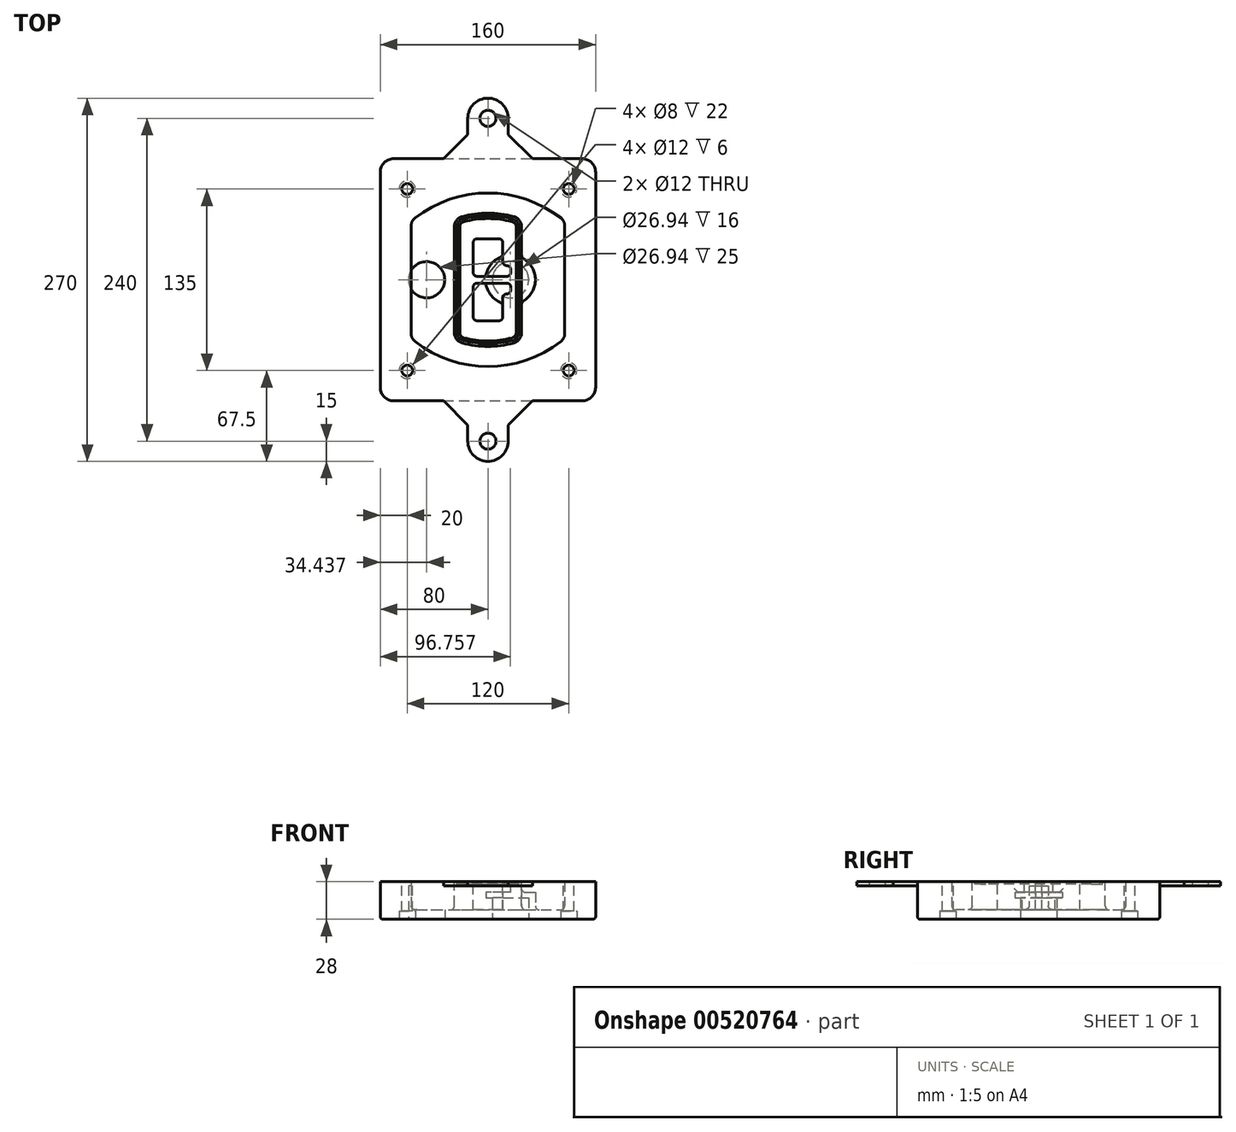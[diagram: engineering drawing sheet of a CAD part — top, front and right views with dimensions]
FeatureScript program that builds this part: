
annotation { "Feature Type Name" : "Feature", "Feature Type Description" : "" }
export const myFeature = defineFeature(function(context is Context, id is Id, definition is map)
    precondition{}
    {
        {
            var Q0;
            Q0=qCreatedBy(makeId("Top.planeOp"),FACE);
            var sketch = newSketch(context, id + "F0", { "sketchPlane" : qUnion([Q0])});
            skPoint(sketch, "E0.rect.middle", {"position": v(0, 0) * mm});
            skLineSegment(sketch, "E1.bottom", {"start": v(-70, -90) * mm, "end": v(70, -90) * mm});
            skLineSegment(sketch, "E1.top", {"start": v(-70, 90) * mm, "end": v(70, 90) * mm});
            skLineSegment(sketch, "E1.left", {"start": v(-80, -80) * mm, "end": v(-80, 80) * mm});
            skLineSegment(sketch, "E1.right", {"start": v(80, -80) * mm, "end": v(80, 80) * mm});
            skLineSegment(sketch, "E2", {"start": v(-80, 90) * mm, "end": v(80, -90) * mm, "construction": true});
            skLineSegment(sketch, "E3", {"start": v(80, 90) * mm, "end": v(-80, -90) * mm, "construction": true});
            skCircle(sketch, "E4", {"center": v(-60, 67.5) * mm, "radius": 4 * mm});
            skCircle(sketch, "E5", {"center": v(60, 67.5) * mm, "radius": 4 * mm});
            skCircle(sketch, "E6", {"center": v(60, -67.5) * mm, "radius": 4 * mm});
            skCircle(sketch, "E7", {"center": v(-60, -67.5) * mm, "radius": 4 * mm});
            skLineSegment(sketch, "E8", {"start": v(-60, 67.5) * mm, "end": v(60, 67.5) * mm, "construction": true});
            skLineSegment(sketch, "E9", {"start": v(60, 67.5) * mm, "end": v(60, -67.5) * mm, "construction": true});
            skLineSegment(sketch, "E10", {"start": v(60, -67.5) * mm, "end": v(-60, -67.5) * mm, "construction": true});
            skLineSegment(sketch, "E11", {"start": v(-60, -67.5) * mm, "end": v(-60, 67.5) * mm, "construction": true});
            skLineSegment(sketch, "E12", {"start": v(-60, 40.3) * mm, "end": v(-60, -40.3) * mm});
            skLineSegment(sketch, "E13", {"start": v(60, 40.3) * mm, "end": v(60, -40.3) * mm});
            skArc(sketch, "E14", {"start": v(56.15, 48.18) * mm, "mid": v(0, 67.5) * mm, "end": v(-56.15, 48.18) * mm});
            skArc(sketch, "E15", {"start": v(-56.15, -48.18) * mm, "mid": v(0, -67.5) * mm, "end": v(56.15, -48.18) * mm});
            skLineSegment(sketch, "E16", {"start": v(-60, 0) * mm, "end": v(60, 0) * mm, "construction": true});
            skPoint(sketch, "E17.visualSharp", {"position": v(-60, -45) * mm});
            skArc(sketch, "E17.filletArc", {"start": v(-60, -40.3) * mm, "mid": v(-58.99, -44.68) * mm, "end": v(-56.15, -48.18) * mm});
            skPoint(sketch, "E18.visualSharp", {"position": v(-60, 45) * mm});
            skArc(sketch, "E18.filletArc", {"start": v(-56.15, 48.18) * mm, "mid": v(-58.99, 44.68) * mm, "end": v(-60, 40.3) * mm});
            skPoint(sketch, "E19.visualSharp", {"position": v(60, 45) * mm});
            skArc(sketch, "E19.filletArc", {"start": v(60, 40.3) * mm, "mid": v(58.99, 44.68) * mm, "end": v(56.15, 48.18) * mm});
            skPoint(sketch, "E20.visualSharp", {"position": v(60, -45) * mm});
            skArc(sketch, "E20.filletArc", {"start": v(56.15, -48.18) * mm, "mid": v(58.99, -44.68) * mm, "end": v(60, -40.3) * mm});
            skPoint(sketch, "E21.visualSharp", {"position": v(-80, 90) * mm});
            skArc(sketch, "E21.filletArc", {"start": v(-70, 90) * mm, "mid": v(-77.07, 87.07) * mm, "end": v(-80, 80) * mm});
            skPoint(sketch, "E22.visualSharp", {"position": v(80, 90) * mm});
            skArc(sketch, "E22.filletArc", {"start": v(80, 80) * mm, "mid": v(77.07, 87.07) * mm, "end": v(70, 90) * mm});
            skPoint(sketch, "E23.visualSharp", {"position": v(80, -90) * mm});
            skArc(sketch, "E23.filletArc", {"start": v(70, -90) * mm, "mid": v(77.07, -87.07) * mm, "end": v(80, -80) * mm});
            skPoint(sketch, "E24.visualSharp", {"position": v(-80, -90) * mm});
            skArc(sketch, "E24.filletArc", {"start": v(-80, -80) * mm, "mid": v(-77.07, -87.07) * mm, "end": v(-70, -90) * mm});
            skArc(sketch, "E25.0", {"start": v(57, 40.3) * mm, "mid": v(56.3, 43.36) * mm, "end": v(54.3, 45.81) * mm});
            skLineSegment(sketch, "E25.1", {"start": v(57, 40.3) * mm, "end": v(57, -40.3) * mm});
            skArc(sketch, "E25.2", {"start": v(54.3, -45.81) * mm, "mid": v(56.3, -43.36) * mm, "end": v(57, -40.3) * mm});
            skArc(sketch, "E25.3", {"start": v(-54.3, -45.81) * mm, "mid": v(0, -64.5) * mm, "end": v(54.3, -45.81) * mm});
            skArc(sketch, "E25.4", {"start": v(-57, -40.3) * mm, "mid": v(-56.3, -43.36) * mm, "end": v(-54.3, -45.81) * mm});
            skArc(sketch, "E25.5", {"start": v(54.3, 45.81) * mm, "mid": v(0, 64.5) * mm, "end": v(-54.3, 45.81) * mm});
            skLineSegment(sketch, "E25.6", {"start": v(-57, 40.3) * mm, "end": v(-57, -40.3) * mm});
            skArc(sketch, "E25.7", {"start": v(-54.3, 45.81) * mm, "mid": v(-56.3, 43.36) * mm, "end": v(-57, 40.3) * mm});
            skArc(sketch, "E26.0", {"start": v(-58.62, 51.33) * mm, "mid": v(-62.58, 46.43) * mm, "end": v(-64, 40.3) * mm});
            skArc(sketch, "E26.1", {"start": v(58.62, 51.33) * mm, "mid": v(0, 71.5) * mm, "end": v(-58.62, 51.33) * mm});
            skArc(sketch, "E26.2", {"start": v(64, 40.3) * mm, "mid": v(62.58, 46.43) * mm, "end": v(58.62, 51.33) * mm});
            skLineSegment(sketch, "E26.3", {"start": v(64, 40.3) * mm, "end": v(64, -40.3) * mm});
            skArc(sketch, "E26.4", {"start": v(58.62, -51.33) * mm, "mid": v(62.58, -46.43) * mm, "end": v(64, -40.3) * mm});
            skLineSegment(sketch, "E26.5", {"start": v(-64, 40.3) * mm, "end": v(-64, -40.3) * mm});
            skArc(sketch, "E26.6", {"start": v(-58.62, -51.33) * mm, "mid": v(0, -71.5) * mm, "end": v(58.62, -51.33) * mm});
            skArc(sketch, "E26.7", {"start": v(-64, -40.3) * mm, "mid": v(-62.58, -46.43) * mm, "end": v(-58.62, -51.33) * mm});
            skSolve(sketch);
        }
        {
            var Q0;
            Q0=makeQuery(id+"F0.imprint","IMPRINT",FACE,{"disambiguationData":[TD([[makeQuery(id+"F0.imprint","IMPRINT",EDGE,{"derivedFrom":sQuery(id+"F0.wireOp",EDGE,"E1.bottom")}),1.0]])]});
            var Q1;
            Q1=makeQuery(id+"F0.imprint","IMPRINT",FACE,{"disambiguationData":[TD([[makeQuery(id+"F0.imprint","IMPRINT",EDGE,{"derivedFrom":sQuery(id+"F0.wireOp",EDGE,"E12")}),1.0]])]});
            var Q2;
            Q2=makeQuery(id+"F0.imprint","IMPRINT",FACE,{"disambiguationData":[TD([[makeQuery(id+"F0.imprint","IMPRINT",EDGE,{"derivedFrom":sQuery(id+"F0.wireOp",EDGE,"E25.0")}),1.0]])]});
            var Q3;
            Q3=makeQuery(id+"F0.imprint","IMPRINT",FACE,{"disambiguationData":[TD([[makeQuery(id+"F0.imprint","IMPRINT",EDGE,{"derivedFrom":sQuery(id+"F0.wireOp",EDGE,"E12")}),-1.0]])]});
            extrude(context, id + "F1", {"entities" : qUnion([Q0, Q1, Q2, Q3]), "oppositeDirection" : true, "depth" : 25 * mm});
        }
        {
            var Q0;
            Q0=makeQuery(id+"F0.imprint","IMPRINT",FACE,{"disambiguationData":[TD([[makeQuery(id+"F0.imprint","IMPRINT",EDGE,{"derivedFrom":sQuery(id+"F0.wireOp",EDGE,"E12")}),1.0]])]});
            extrude(context, id + "F2", {"entities" : qUnion([Q0]), "operationType" : NewBodyOperationType.ADD, "depth" : 3 * mm, "offsetDistance" : 25 * mm});
        }
        {
            var Q0;
            Q0=makeQuery(id+"F0.imprint","IMPRINT",FACE,{"disambiguationData":[TD([[makeQuery(id+"F0.imprint","IMPRINT",EDGE,{"derivedFrom":sQuery(id+"F0.wireOp",EDGE,"E25.0")}),1.0]])]});
            extrude(context, id + "F3", {"entities" : qUnion([Q0]), "operationType" : NewBodyOperationType.REMOVE, "oppositeDirection" : true, "depth" : 18 * mm});
        }
        {
            var Q0;
            Q0=makeQuery(id+"F2.opExtrude","CAP_FACE",FACE,{"disambiguationData":[OSD([sQuery(id+"F0.wireOp",EDGE,"E12"),sQuery(id+"F0.wireOp",EDGE,"E13"),sQuery(id+"F0.wireOp",EDGE,"E14"),sQuery(id+"F0.wireOp",EDGE,"E15"),sQuery(id+"F0.wireOp",EDGE,"E17.filletArc"),sQuery(id+"F0.wireOp",EDGE,"E18.filletArc"),sQuery(id+"F0.wireOp",EDGE,"E19.filletArc"),sQuery(id+"F0.wireOp",EDGE,"E20.filletArc"),sQuery(id+"F0.wireOp",EDGE,"E25.0"),sQuery(id+"F0.wireOp",EDGE,"E25.1"),sQuery(id+"F0.wireOp",EDGE,"E25.2"),sQuery(id+"F0.wireOp",EDGE,"E25.3"),sQuery(id+"F0.wireOp",EDGE,"E25.4"),sQuery(id+"F0.wireOp",EDGE,"E25.5"),sQuery(id+"F0.wireOp",EDGE,"E25.6"),sQuery(id+"F0.wireOp",EDGE,"E25.7")])],"isStart":false});
            var sketch = newSketch(context, id + "F4", { "sketchPlane" : qUnion([Q0])});
            skArc(sketch, "E27.0", {"start": v(-19.08, -46.97) * mm, "mid": v(0, -49.5) * mm, "end": v(19.08, -46.97) * mm});
            skArc(sketch, "E28.0", {"start": v(19.08, 46.97) * mm, "mid": v(0, 49.5) * mm, "end": v(-19.08, 46.97) * mm});
            skLineSegment(sketch, "E29", {"start": v(-25, 39.25) * mm, "end": v(-25, -39.25) * mm});
            skLineSegment(sketch, "E30", {"start": v(25, 39.25) * mm, "end": v(25, -39.25) * mm});
            skLineSegment(sketch, "E31", {"start": v(-25, 45.1) * mm, "end": v(25, 45.1) * mm, "construction": true});
            skLineSegment(sketch, "E32", {"start": v(-25, -45.1) * mm, "end": v(25, -45.1) * mm, "construction": true});
            skPoint(sketch, "E33.visualSharp", {"position": v(-25, 45.1) * mm});
            skArc(sketch, "E33.filletArc", {"start": v(-19.08, 46.97) * mm, "mid": v(-23.35, 44.11) * mm, "end": v(-25, 39.25) * mm});
            skPoint(sketch, "E34.visualSharp", {"position": v(25, 45.1) * mm});
            skArc(sketch, "E34.filletArc", {"start": v(25, 39.25) * mm, "mid": v(23.35, 44.11) * mm, "end": v(19.08, 46.97) * mm});
            skPoint(sketch, "E35.visualSharp", {"position": v(25, -45.1) * mm});
            skArc(sketch, "E35.filletArc", {"start": v(19.08, -46.97) * mm, "mid": v(23.35, -44.11) * mm, "end": v(25, -39.25) * mm});
            skPoint(sketch, "E36.visualSharp", {"position": v(-25, -45.1) * mm});
            skArc(sketch, "E36.filletArc", {"start": v(-25, -39.25) * mm, "mid": v(-23.35, -44.11) * mm, "end": v(-19.08, -46.97) * mm});
            skArc(sketch, "E37.0", {"start": v(54.3, 45.81) * mm, "mid": v(0, 64.5) * mm, "end": v(-54.3, 45.81) * mm});
            skArc(sketch, "E37.1", {"start": v(-54.3, 45.81) * mm, "mid": v(-56.3, 43.36) * mm, "end": v(-57, 40.3) * mm});
            skLineSegment(sketch, "E37.2", {"start": v(-57, 40.3) * mm, "end": v(-57, -40.3) * mm});
            skArc(sketch, "E37.3", {"start": v(-57, -40.3) * mm, "mid": v(-56.3, -43.36) * mm, "end": v(-54.3, -45.81) * mm});
            skArc(sketch, "E37.4", {"start": v(-54.3, -45.81) * mm, "mid": v(0, -64.5) * mm, "end": v(54.3, -45.81) * mm});
            skArc(sketch, "E37.5", {"start": v(54.3, -45.81) * mm, "mid": v(56.3, -43.36) * mm, "end": v(57, -40.3) * mm});
            skLineSegment(sketch, "E37.6", {"start": v(57, 40.3) * mm, "end": v(57, -40.3) * mm});
            skArc(sketch, "E37.7", {"start": v(57, 40.3) * mm, "mid": v(56.3, 43.36) * mm, "end": v(54.3, 45.81) * mm});
            skLineSegment(sketch, "E38.0", {"start": v(23, 39.25) * mm, "end": v(23, -39.25) * mm});
            skArc(sketch, "E38.1", {"start": v(18.56, -45.04) * mm, "mid": v(21.76, -42.9) * mm, "end": v(23, -39.25) * mm});
            skArc(sketch, "E38.2", {"start": v(-18.56, -45.04) * mm, "mid": v(0, -47.5) * mm, "end": v(18.56, -45.04) * mm});
            skArc(sketch, "E38.3", {"start": v(-23, -39.25) * mm, "mid": v(-21.76, -42.9) * mm, "end": v(-18.56, -45.04) * mm});
            skLineSegment(sketch, "E38.4", {"start": v(-23, 39.25) * mm, "end": v(-23, -39.25) * mm});
            skArc(sketch, "E38.5", {"start": v(23, 39.25) * mm, "mid": v(21.76, 42.9) * mm, "end": v(18.56, 45.04) * mm});
            skArc(sketch, "E38.6", {"start": v(-18.56, 45.04) * mm, "mid": v(-21.76, 42.9) * mm, "end": v(-23, 39.25) * mm});
            skArc(sketch, "E38.7", {"start": v(18.56, 45.04) * mm, "mid": v(0, 47.5) * mm, "end": v(-18.56, 45.04) * mm});
            skArc(sketch, "E39.0", {"start": v(21, 39.25) * mm, "mid": v(20.18, 41.68) * mm, "end": v(18.04, 43.1) * mm});
            skLineSegment(sketch, "E39.1", {"start": v(21, 39.25) * mm, "end": v(21, -39.25) * mm});
            skArc(sketch, "E39.2", {"start": v(18.04, -43.1) * mm, "mid": v(20.18, -41.68) * mm, "end": v(21, -39.25) * mm});
            skArc(sketch, "E39.3", {"start": v(-18.04, -43.1) * mm, "mid": v(0, -45.5) * mm, "end": v(18.04, -43.1) * mm});
            skArc(sketch, "E39.4", {"start": v(-21, -39.25) * mm, "mid": v(-20.18, -41.68) * mm, "end": v(-18.04, -43.1) * mm});
            skArc(sketch, "E39.5", {"start": v(18.04, 43.1) * mm, "mid": v(0, 45.5) * mm, "end": v(-18.04, 43.1) * mm});
            skLineSegment(sketch, "E39.6", {"start": v(-21, 39.25) * mm, "end": v(-21, -39.25) * mm});
            skArc(sketch, "E39.7", {"start": v(-18.04, 43.1) * mm, "mid": v(-20.18, 41.68) * mm, "end": v(-21, 39.25) * mm});
            skLineSegment(sketch, "E40", {"start": v(-25, 0) * mm, "end": v(25, 0) * mm, "construction": true});
            skLineSegment(sketch, "E41", {"start": v(-11, 5.5) * mm, "end": v(-11, 27.5) * mm});
            skLineSegment(sketch, "E42", {"start": v(-8, 30.5) * mm, "end": v(8, 30.5) * mm});
            skLineSegment(sketch, "E43", {"start": v(11, 27.5) * mm, "end": v(11, 13.5) * mm});
            skLineSegment(sketch, "E44", {"start": v(14, 10.5) * mm, "end": v(14, 10.5) * mm});
            skLineSegment(sketch, "E45", {"start": v(17, 7.5) * mm, "end": v(17, 5.5) * mm});
            skLineSegment(sketch, "E46", {"start": v(14, 2.5) * mm, "end": v(-8, 2.5) * mm});
            skPoint(sketch, "E47.visualSharp", {"position": v(-11, 30.5) * mm});
            skArc(sketch, "E47.filletArc", {"start": v(-8, 30.5) * mm, "mid": v(-10.12, 29.62) * mm, "end": v(-11, 27.5) * mm});
            skPoint(sketch, "E48.visualSharp", {"position": v(11, 30.5) * mm});
            skArc(sketch, "E48.filletArc", {"start": v(11, 27.5) * mm, "mid": v(10.12, 29.62) * mm, "end": v(8, 30.5) * mm});
            skPoint(sketch, "E49.visualSharp", {"position": v(11, 10.5) * mm});
            skArc(sketch, "E49.filletArc", {"start": v(11, 13.5) * mm, "mid": v(11.88, 11.38) * mm, "end": v(14, 10.5) * mm});
            skPoint(sketch, "E50.visualSharp", {"position": v(17, 10.5) * mm});
            skArc(sketch, "E50.filletArc", {"start": v(17, 7.5) * mm, "mid": v(16.12, 9.62) * mm, "end": v(14, 10.5) * mm});
            skPoint(sketch, "E51.visualSharp", {"position": v(17, 2.5) * mm});
            skArc(sketch, "E51.filletArc", {"start": v(14, 2.5) * mm, "mid": v(16.12, 3.38) * mm, "end": v(17, 5.5) * mm});
            skPoint(sketch, "E52.visualSharp", {"position": v(-11, 2.5) * mm});
            skArc(sketch, "E52.filletArc", {"start": v(-11, 5.5) * mm, "mid": v(-10.12, 3.38) * mm, "end": v(-8, 2.5) * mm});
            skLineSegment(sketch, "E53.0.MirrorCS", {"start": v(14, -2.5) * mm, "end": v(-8, -2.5) * mm});
            skArc(sketch, "E54.0.MirrorCS", {"start": v(-11, -5.5) * mm, "mid": v(-10.12, -3.38) * mm, "end": v(-8, -2.5) * mm});
            skLineSegment(sketch, "E55.0.MirrorCS", {"start": v(-11, -5.5) * mm, "end": v(-11, -27.5) * mm});
            skArc(sketch, "E56.0.MirrorCS", {"start": v(-8, -30.5) * mm, "mid": v(-10.12, -29.62) * mm, "end": v(-11, -27.5) * mm});
            skLineSegment(sketch, "E57.0.MirrorCS", {"start": v(-8, -30.5) * mm, "end": v(8, -30.5) * mm});
            skArc(sketch, "E58.0.MirrorCS", {"start": v(11, -27.5) * mm, "mid": v(10.12, -29.62) * mm, "end": v(8, -30.5) * mm});
            skLineSegment(sketch, "E59.0.MirrorCS", {"start": v(11, -27.5) * mm, "end": v(11, -13.5) * mm});
            skArc(sketch, "E60.0.MirrorCS", {"start": v(11, -13.5) * mm, "mid": v(11.88, -11.38) * mm, "end": v(14, -10.5) * mm});
            skArc(sketch, "E61.0.MirrorCS", {"start": v(17, -7.5) * mm, "mid": v(16.12, -9.62) * mm, "end": v(14, -10.5) * mm});
            skLineSegment(sketch, "E62.0.MirrorCS", {"start": v(17, -7.5) * mm, "end": v(17, -5.5) * mm});
            skArc(sketch, "E63.0.MirrorCS", {"start": v(14, -2.5) * mm, "mid": v(16.12, -3.38) * mm, "end": v(17, -5.5) * mm});
            skSolve(sketch);
        }
        {
            var Q0;
            Q0=makeQuery(id+"F4.imprint","IMPRINT",FACE,{"disambiguationData":[TD([[makeQuery(id+"F4.imprint","IMPRINT",EDGE,{"derivedFrom":sQuery(id+"F4.wireOp",EDGE,"E27.0")}),1.0]])]});
            var Q1;
            Q1=makeQuery(id+"F4.imprint","IMPRINT",FACE,{"disambiguationData":[TD([[makeQuery(id+"F4.imprint","IMPRINT",EDGE,{"derivedFrom":sQuery(id+"F4.wireOp",EDGE,"E38.0")}),-1.0]])]});
            var Q2;
            Q2=makeQuery(id+"F4.imprint","IMPRINT",FACE,{"disambiguationData":[TD([[makeQuery(id+"F4.imprint","IMPRINT",EDGE,{"derivedFrom":sQuery(id+"F4.wireOp",EDGE,"E39.0")}),1.0]])]});
            extrude(context, id + "F5", {"entities" : qUnion([Q0, Q1, Q2]), "operationType" : NewBodyOperationType.ADD, "endBound" : BoundingType.UP_TO_NEXT, "oppositeDirection" : true, "depth" : 25 * mm});
        }
        {
            var Q0;
            Q0=makeQuery(id+"F4.imprint","IMPRINT",FACE,{"disambiguationData":[TD([[makeQuery(id+"F4.imprint","IMPRINT",EDGE,{"derivedFrom":sQuery(id+"F4.wireOp",EDGE,"E38.0")}),-1.0]])]});
            extrude(context, id + "F6", {"entities" : qUnion([Q0]), "operationType" : NewBodyOperationType.REMOVE, "oppositeDirection" : true, "depth" : 2 * mm});
        }
        {
            var Q0;
            Q0=makeQuery(id+"F1.opExtrude","CAP_FACE",FACE,{"disambiguationData":[OSD([sQuery(id+"F0.wireOp",EDGE,"E1.bottom"),sQuery(id+"F0.wireOp",EDGE,"E1.top"),sQuery(id+"F0.wireOp",EDGE,"E1.left"),sQuery(id+"F0.wireOp",EDGE,"E1.right"),sQuery(id+"F0.wireOp",EDGE,"E4"),sQuery(id+"F0.wireOp",EDGE,"E5"),sQuery(id+"F0.wireOp",EDGE,"E6"),sQuery(id+"F0.wireOp",EDGE,"E7"),sQuery(id+"F0.wireOp",EDGE,"E21.filletArc"),sQuery(id+"F0.wireOp",EDGE,"E22.filletArc"),sQuery(id+"F0.wireOp",EDGE,"E23.filletArc"),sQuery(id+"F0.wireOp",EDGE,"E24.filletArc")])],"isStart":false});
            var sketch = newSketch(context, id + "F7", { "sketchPlane" : qUnion([Q0])});
            skCircle(sketch, "E64", {"center": v(16.76, 0) * mm, "radius": 13.47 * mm});
            skCircle(sketch, "E65", {"center": v(-45.56, 0) * mm, "radius": 13.47 * mm});
            skLineSegment(sketch, "E66", {"start": v(80, 0) * mm, "end": v(-80, 0) * mm});
            skCircle(sketch, "E67", {"center": v(16.76, 0) * mm, "radius": 18.47 * mm});
            skCircle(sketch, "E68", {"center": v(60, -67.5) * mm, "radius": 6 * mm});
            skCircle(sketch, "E69", {"center": v(-60, -67.5) * mm, "radius": 6 * mm});
            skCircle(sketch, "E70", {"center": v(-60, 67.5) * mm, "radius": 6 * mm});
            skCircle(sketch, "E71", {"center": v(60, 67.5) * mm, "radius": 6 * mm});
            skSolve(sketch);
        }
        {
            var Q0;
            {var subQ1=sQuery(id+"F7.wireOp",EDGE,"E66");var subQ4=sQuery(id+"F7.wireOp",EDGE,"E64");var subQ6=makeQuery(id+"F7.imprint","INTERSECT",VERTEX,{"disambiguationData":[OD(0.0)],"derivedFrom":[subQ4,subQ1]});Q0=makeQuery(id+"F7.imprint","IMPRINT",FACE,{"disambiguationData":[TD([[makeQuery(id+"F7.imprint","IMPRINT",EDGE,{"disambiguationData":[TD([[subQ6,-1.0]])],"derivedFrom":subQ4}),-1.0]])]});}
            var Q1;
            {var subQ0=sQuery(id+"F7.wireOp",EDGE,"E66");var subQ1=sQuery(id+"F7.wireOp",EDGE,"E64");var subQ3=makeQuery(id+"F7.imprint","INTERSECT",VERTEX,{"disambiguationData":[OD(0.0)],"derivedFrom":[subQ1,subQ0]});Q1=makeQuery(id+"F7.imprint","IMPRINT",FACE,{"disambiguationData":[TD([[makeQuery(id+"F7.imprint","IMPRINT",EDGE,{"disambiguationData":[TD([[subQ3,-1.0]])],"derivedFrom":subQ1}),1.0]])]});}
            var Q2;
            {var subQ0=sQuery(id+"F7.wireOp",EDGE,"E66");var subQ1=sQuery(id+"F7.wireOp",EDGE,"E64");var subQ3=makeQuery(id+"F7.imprint","INTERSECT",VERTEX,{"disambiguationData":[OD(0.0)],"derivedFrom":[subQ1,subQ0]});Q2=makeQuery(id+"F7.imprint","IMPRINT",FACE,{"disambiguationData":[TD([[makeQuery(id+"F7.imprint","IMPRINT",EDGE,{"disambiguationData":[TD([[subQ3,1.0]])],"derivedFrom":subQ1}),1.0]])]});}
            var Q3;
            {var subQ1=sQuery(id+"F7.wireOp",EDGE,"E66");var subQ4=sQuery(id+"F7.wireOp",EDGE,"E64");var subQ6=makeQuery(id+"F7.imprint","INTERSECT",VERTEX,{"disambiguationData":[OD(0.0)],"derivedFrom":[subQ4,subQ1]});Q3=makeQuery(id+"F7.imprint","IMPRINT",FACE,{"disambiguationData":[TD([[makeQuery(id+"F7.imprint","IMPRINT",EDGE,{"disambiguationData":[TD([[subQ6,1.0]])],"derivedFrom":subQ4}),-1.0]])]});}
            extrude(context, id + "F8", {"entities" : qUnion([Q0, Q1, Q2, Q3]), "operationType" : NewBodyOperationType.ADD, "oppositeDirection" : true, "depth" : 20 * mm});
        }
        {
            var Q0;
            {var subQ0=sQuery(id+"F7.wireOp",EDGE,"E66");var subQ1=sQuery(id+"F7.wireOp",EDGE,"E64");var subQ3=makeQuery(id+"F7.imprint","INTERSECT",VERTEX,{"disambiguationData":[OD(0.0)],"derivedFrom":[subQ1,subQ0]});Q0=makeQuery(id+"F7.imprint","IMPRINT",FACE,{"disambiguationData":[TD([[makeQuery(id+"F7.imprint","IMPRINT",EDGE,{"disambiguationData":[TD([[subQ3,-1.0]])],"derivedFrom":subQ1}),1.0]])]});}
            var Q1;
            {var subQ0=sQuery(id+"F7.wireOp",EDGE,"E66");var subQ1=sQuery(id+"F7.wireOp",EDGE,"E64");var subQ3=makeQuery(id+"F7.imprint","INTERSECT",VERTEX,{"disambiguationData":[OD(0.0)],"derivedFrom":[subQ1,subQ0]});Q1=makeQuery(id+"F7.imprint","IMPRINT",FACE,{"disambiguationData":[TD([[makeQuery(id+"F7.imprint","IMPRINT",EDGE,{"disambiguationData":[TD([[subQ3,1.0]])],"derivedFrom":subQ1}),1.0]])]});}
            extrude(context, id + "F9", {"entities" : qUnion([Q0, Q1]), "operationType" : NewBodyOperationType.REMOVE, "oppositeDirection" : true, "depth" : 16 * mm});
        }
        {
            var Q0;
            {var subQ0=sQuery(id+"F7.wireOp",EDGE,"E66");var subQ1=sQuery(id+"F7.wireOp",EDGE,"E65");var subQ3=makeQuery(id+"F7.imprint","INTERSECT",VERTEX,{"disambiguationData":[OD(0.0)],"derivedFrom":[subQ1,subQ0]});Q0=makeQuery(id+"F7.imprint","IMPRINT",FACE,{"disambiguationData":[TD([[makeQuery(id+"F7.imprint","IMPRINT",EDGE,{"disambiguationData":[TD([[subQ3,-1.0]])],"derivedFrom":subQ1}),1.0]])]});}
            var Q1;
            {var subQ0=sQuery(id+"F7.wireOp",EDGE,"E66");var subQ1=sQuery(id+"F7.wireOp",EDGE,"E65");var subQ3=makeQuery(id+"F7.imprint","INTERSECT",VERTEX,{"disambiguationData":[OD(0.0)],"derivedFrom":[subQ1,subQ0]});Q1=makeQuery(id+"F7.imprint","IMPRINT",FACE,{"disambiguationData":[TD([[makeQuery(id+"F7.imprint","IMPRINT",EDGE,{"disambiguationData":[TD([[subQ3,1.0]])],"derivedFrom":subQ1}),1.0]])]});}
            extrude(context, id + "F10", {"entities" : qUnion([Q0, Q1]), "operationType" : NewBodyOperationType.REMOVE, "oppositeDirection" : true, "depth" : 25 * mm});
        }
        {
            var Q0;
            Q0=makeQuery(id+"F7.imprint","IMPRINT",FACE,{"disambiguationData":[TD([[makeQuery(id+"F7.imprint","IMPRINT",EDGE,{"derivedFrom":sQuery(id+"F7.wireOp",EDGE,"E68")}),1.0]])]});
            var Q1;
            Q1=makeQuery(id+"F7.imprint","IMPRINT",FACE,{"disambiguationData":[TD([[makeQuery(id+"F7.imprint","IMPRINT",EDGE,{"derivedFrom":makeQuery(id+"F1.opExtrude","CAP_EDGE",EDGE,{"disambiguationData":[OSD([sQuery(id+"F0.wireOp",EDGE,"E5")])],"isStart":false})}),-1.0]])]});
            var Q2;
            Q2=makeQuery(id+"F7.imprint","IMPRINT",FACE,{"disambiguationData":[TD([[makeQuery(id+"F7.imprint","IMPRINT",EDGE,{"derivedFrom":sQuery(id+"F7.wireOp",EDGE,"E69")}),1.0]])]});
            var Q3;
            Q3=makeQuery(id+"F7.imprint","IMPRINT",FACE,{"disambiguationData":[TD([[makeQuery(id+"F7.imprint","IMPRINT",EDGE,{"derivedFrom":makeQuery(id+"F1.opExtrude","CAP_EDGE",EDGE,{"disambiguationData":[OSD([sQuery(id+"F0.wireOp",EDGE,"E4")])],"isStart":false})}),-1.0]])]});
            var Q4;
            Q4=makeQuery(id+"F7.imprint","IMPRINT",FACE,{"disambiguationData":[TD([[makeQuery(id+"F7.imprint","IMPRINT",EDGE,{"derivedFrom":sQuery(id+"F7.wireOp",EDGE,"E70")}),1.0]])]});
            var Q5;
            Q5=makeQuery(id+"F7.imprint","IMPRINT",FACE,{"disambiguationData":[TD([[makeQuery(id+"F7.imprint","IMPRINT",EDGE,{"derivedFrom":makeQuery(id+"F1.opExtrude","CAP_EDGE",EDGE,{"disambiguationData":[OSD([sQuery(id+"F0.wireOp",EDGE,"E7")])],"isStart":false})}),-1.0]])]});
            var Q6;
            Q6=makeQuery(id+"F7.imprint","IMPRINT",FACE,{"disambiguationData":[TD([[makeQuery(id+"F7.imprint","IMPRINT",EDGE,{"derivedFrom":sQuery(id+"F7.wireOp",EDGE,"E71")}),1.0]])]});
            var Q7;
            Q7=makeQuery(id+"F7.imprint","IMPRINT",FACE,{"disambiguationData":[TD([[makeQuery(id+"F7.imprint","IMPRINT",EDGE,{"derivedFrom":makeQuery(id+"F1.opExtrude","CAP_EDGE",EDGE,{"disambiguationData":[OSD([sQuery(id+"F0.wireOp",EDGE,"E6")])],"isStart":false})}),-1.0]])]});
            extrude(context, id + "F11", {"entities" : qUnion([Q0, Q1, Q2, Q3, Q4, Q5, Q6, Q7]), "operationType" : NewBodyOperationType.REMOVE, "oppositeDirection" : true, "depth" : 6 * mm});
        }
        {
            var Q0;
            Q0=makeQuery(id+"F9.boolean.opBoolean","COPY",FACE,{"derivedFrom":makeQuery(id+"F9.opExtrude","CAP_FACE",FACE,{"disambiguationData":[OSD([sQuery(id+"F7.wireOp",EDGE,"E64")])],"isStart":false})});
            var sketch = newSketch(context, id + "F12", { "sketchPlane" : qUnion([Q0])});
            skArc(sketch, "E72.0", {"start": v(11, 17.55) * mm, "mid": v(2.57, 11.82) * mm, "end": v(-1.54, 2.5) * mm});
            skArc(sketch, "E72.1", {"start": v(-1.54, -2.5) * mm, "mid": v(2.57, -11.82) * mm, "end": v(11, -17.55) * mm});
            skLineSegment(sketch, "E73", {"start": v(-1.54, -2.5) * mm, "end": v(14, -2.5) * mm});
            skLineSegment(sketch, "E74.0", {"start": v(14, 2.5) * mm, "end": v(-1.54, 2.5) * mm});
            skArc(sketch, "E74.1", {"start": v(14, 2.5) * mm, "mid": v(16.12, 3.38) * mm, "end": v(17, 5.5) * mm});
            skLineSegment(sketch, "E74.2", {"start": v(17, 7.5) * mm, "end": v(17, 5.5) * mm});
            skArc(sketch, "E74.3", {"start": v(17, 7.5) * mm, "mid": v(16.12, 9.62) * mm, "end": v(14, 10.5) * mm});
            skArc(sketch, "E74.4", {"start": v(11, 13.5) * mm, "mid": v(11.88, 11.38) * mm, "end": v(14, 10.5) * mm});
            skLineSegment(sketch, "E74.5", {"start": v(11, 17.55) * mm, "end": v(11, 13.5) * mm});
            skLineSegment(sketch, "E74.7", {"start": v(14, -2.5) * mm, "end": v(-1.54, -2.5) * mm});
            skArc(sketch, "E74.8", {"start": v(14, -2.5) * mm, "mid": v(16.12, -3.38) * mm, "end": v(17, -5.5) * mm});
            skLineSegment(sketch, "E74.9", {"start": v(17, -7.5) * mm, "end": v(17, -5.5) * mm});
            skArc(sketch, "E74.10", {"start": v(17, -7.5) * mm, "mid": v(16.12, -9.62) * mm, "end": v(14, -10.5) * mm});
            skArc(sketch, "E74.11", {"start": v(11, -13.5) * mm, "mid": v(11.88, -11.38) * mm, "end": v(14, -10.5) * mm});
            skLineSegment(sketch, "E74.12", {"start": v(11, -17.55) * mm, "end": v(11, -13.5) * mm});
            skPoint(sketch, "E75.orphan", {"position": v(11, -27.5) * mm});
            skPoint(sketch, "E76.orphan", {"position": v(-8, -2.5) * mm});
            skPoint(sketch, "E77.orphan", {"position": v(-8, 2.5) * mm});
            skPoint(sketch, "E78.orphan", {"position": v(11, 27.5) * mm});
            skSolve(sketch);
        }
        {
            var Q0;
            {var subQ7=sQuery(id+"F12.wireOp",EDGE,"E72.0");var subQ14=sQuery(id+"F12.wireOp",EDGE,"E72.1");var subQ16=sQuery(id+"F12.wireOp",EDGE,"E74.1");var subQ18=sQuery(id+"F12.wireOp",EDGE,"E74.8");Q0=qUnion([makeQuery(id+"F12.imprint","IMPRINT",FACE,{"disambiguationData":[TD([[makeQuery(id+"F12.imprint","IMPRINT",EDGE,{"derivedFrom":subQ7}),1.0]])]}),makeQuery(id+"F12.imprint","IMPRINT",FACE,{"disambiguationData":[TD([[makeQuery(id+"F12.imprint","IMPRINT",EDGE,{"derivedFrom":subQ14}),1.0]])]}),makeQuery(id+"F12.imprint","IMPRINT",FACE,{"disambiguationData":[TD([[makeQuery(id+"F12.imprint","IMPRINT",EDGE,{"derivedFrom":subQ16}),1.0]])]}),makeQuery(id+"F12.imprint","IMPRINT",FACE,{"disambiguationData":[TD([[makeQuery(id+"F12.imprint","IMPRINT",EDGE,{"derivedFrom":subQ18}),-1.0]])]})]);}
            var Q1;
            Q1=makeQuery(id+"F5.boolean.opBoolean","SPLIT",FACE,{"disambiguationData":[TD([makeQuery(id+"F5.opExtrude","SWEPT_FACE",FACE,{"disambiguationData":[OSD([sQuery(id+"F4.wireOp",EDGE,"E41")])]})])],"derivedFrom":makeQuery(id+"F3.boolean.opBoolean","COPY",FACE,{"derivedFrom":makeQuery(id+"F3.opExtrude","CAP_FACE",FACE,{"disambiguationData":[OSD([sQuery(id+"F0.wireOp",EDGE,"E25.0"),sQuery(id+"F0.wireOp",EDGE,"E25.1"),sQuery(id+"F0.wireOp",EDGE,"E25.2"),sQuery(id+"F0.wireOp",EDGE,"E25.3"),sQuery(id+"F0.wireOp",EDGE,"E25.4"),sQuery(id+"F0.wireOp",EDGE,"E25.5"),sQuery(id+"F0.wireOp",EDGE,"E25.6"),sQuery(id+"F0.wireOp",EDGE,"E25.7")])],"isStart":false})})});
            extrude(context, id + "F13", {"entities" : qUnion([Q0]), "operationType" : NewBodyOperationType.REMOVE, "endBound" : BoundingType.UP_TO_SURFACE, "endBoundEntityFace" : qUnion([Q1]), "depth" : 25 * mm});
        }
        {
            var Q0;
            Q0=makeQuery(id+"F3.boolean.opBoolean","COPY",EDGE,{"derivedFrom":makeQuery(id+"F3.opExtrude","CAP_EDGE",EDGE,{"disambiguationData":[OSD([sQuery(id+"F0.wireOp",EDGE,"E25.6")])],"isStart":false})});
            var Q1;
            Q1=makeQuery(id+"F8.boolean.opBoolean","INTERSECT",EDGE,{"derivedFrom":[makeQuery(id+"F5.opExtrude","SWEPT_FACE",FACE,{"disambiguationData":[OSD([sQuery(id+"F4.wireOp",EDGE,"E30")])]}),makeQuery(id+"F8.opExtrude","CAP_FACE",FACE,{"disambiguationData":[OSD([sQuery(id+"F7.wireOp",EDGE,"E67")])],"isStart":false})]});
            var Q2;
            Q2=makeQuery(id+"F8.boolean.opBoolean","INTERSECT",EDGE,{"disambiguationData":[OD(1.0)],"derivedFrom":[makeQuery(id+"F5.opExtrude","SWEPT_FACE",FACE,{"disambiguationData":[OSD([sQuery(id+"F4.wireOp",EDGE,"E30")])]}),makeQuery(id+"F8.opExtrude","SWEPT_FACE",FACE,{"disambiguationData":[OSD([sQuery(id+"F7.wireOp",EDGE,"E67")])]})]});
            var Q3;
            {var subQ0=sQuery(id+"F4.wireOp",EDGE,"E30");Q3=makeQuery(id+"F8.boolean.opBoolean","SPLIT",EDGE,{"disambiguationData":[TD([makeQuery(id+"F5.opExtrude","SWEPT_FACE",FACE,{"disambiguationData":[OSD([sQuery(id+"F4.wireOp",EDGE,"E35.filletArc")])]})])],"derivedFrom":makeQuery(id+"F5.opExtrude","CAP_EDGE",EDGE,{"disambiguationData":[OSD([subQ0])],"isStart":false})});}
            var Q4;
            {var subQ0=sQuery(id+"F0.wireOp",EDGE,"E25.7");var subQ1=sQuery(id+"F0.wireOp",EDGE,"E25.1");var subQ2=sQuery(id+"F0.wireOp",EDGE,"E25.6");var subQ3=sQuery(id+"F0.wireOp",EDGE,"E25.5");var subQ4=sQuery(id+"F0.wireOp",EDGE,"E25.4");var subQ5=sQuery(id+"F0.wireOp",EDGE,"E25.0");var subQ6=sQuery(id+"F0.wireOp",EDGE,"E25.2");var subQ7=sQuery(id+"F0.wireOp",EDGE,"E25.3");Q4=makeQuery(id+"F8.boolean.opBoolean","INTERSECT",EDGE,{"derivedFrom":[makeQuery(id+"F5.boolean.opBoolean","SPLIT",FACE,{"disambiguationData":[TD([makeQuery(id+"F2.opExtrude","SWEPT_FACE",FACE,{"disambiguationData":[OSD([subQ5])]})])],"derivedFrom":makeQuery(id+"F3.boolean.opBoolean","COPY",FACE,{"derivedFrom":makeQuery(id+"F3.opExtrude","CAP_FACE",FACE,{"disambiguationData":[OSD([subQ5,subQ1,subQ6,subQ7,subQ4,subQ3,subQ2,subQ0])],"isStart":false})})}),makeQuery(id+"F8.opExtrude","SWEPT_FACE",FACE,{"disambiguationData":[OSD([sQuery(id+"F7.wireOp",EDGE,"E67")])]})]});}
            var Q5;
            Q5=makeQuery(id+"F8.boolean.opBoolean","INTERSECT",EDGE,{"disambiguationData":[OD(0.0)],"derivedFrom":[makeQuery(id+"F5.opExtrude","SWEPT_FACE",FACE,{"disambiguationData":[OSD([sQuery(id+"F4.wireOp",EDGE,"E30")])]}),makeQuery(id+"F8.opExtrude","SWEPT_FACE",FACE,{"disambiguationData":[OSD([sQuery(id+"F7.wireOp",EDGE,"E67")])]})]});
            fillet(context, id + "F14", {"entities" : qUnion([Q0, Q1, Q2, Q3, Q4, Q5]), "radius" : 3 * mm, "tangentPropagation" : true, "allowEdgeOverflow" : false});
        }
        {
            var Q0;
            Q0=makeQuery(id+"F1.opExtrude","CAP_EDGE",EDGE,{"disambiguationData":[OSD([sQuery(id+"F0.wireOp",EDGE,"E1.bottom")])],"isStart":false});
            fillet(context, id + "F15", {"entities" : qUnion([Q0]), "radius" : 2 * mm, "tangentPropagation" : true, "allowEdgeOverflow" : false});
        }
        {
            var Q0;
            {var subQ0=sQuery(id+"F0.wireOp",EDGE,"E21.filletArc");var subQ1=sQuery(id+"F0.wireOp",EDGE,"E7");var subQ2=sQuery(id+"F0.wireOp",EDGE,"E6");var subQ3=sQuery(id+"F0.wireOp",EDGE,"E5");var subQ4=sQuery(id+"F0.wireOp",EDGE,"E4");var subQ5=sQuery(id+"F0.wireOp",EDGE,"E22.filletArc");var subQ6=sQuery(id+"F0.wireOp",EDGE,"E1.bottom");var subQ7=sQuery(id+"F0.wireOp",EDGE,"E1.right");var subQ8=sQuery(id+"F0.wireOp",EDGE,"E1.top");var subQ9=sQuery(id+"F0.wireOp",EDGE,"E1.left");var subQ10=sQuery(id+"F0.wireOp",EDGE,"E23.filletArc");var subQ11=sQuery(id+"F0.wireOp",EDGE,"E24.filletArc");Q0=makeQuery(id+"F2.boolean.opBoolean","SPLIT",FACE,{"disambiguationData":[TD([makeQuery(id+"F1.opExtrude","SWEPT_FACE",FACE,{"disambiguationData":[OSD([subQ6])]})])],"derivedFrom":makeQuery(id+"F1.opExtrude","CAP_FACE",FACE,{"disambiguationData":[OSD([subQ6,subQ8,subQ9,subQ7,subQ4,subQ3,subQ2,subQ1,subQ0,subQ5,subQ10,subQ11])],"isStart":true})});}
            var sketch = newSketch(context, id + "F16", { "sketchPlane" : qUnion([Q0])});
            skCircle(sketch, "E79", {"center": v(0, 120) * mm, "radius": 6 * mm});
            skLineSegment(sketch, "E80", {"start": v(-15, 108) * mm, "end": v(-33, 90) * mm});
            skLineSegment(sketch, "E81", {"start": v(-15, 108) * mm, "end": v(-15, 120) * mm});
            skLineSegment(sketch, "E82", {"start": v(33, 90) * mm, "end": v(15, 108) * mm});
            skLineSegment(sketch, "E83", {"start": v(15, 108) * mm, "end": v(15, 120) * mm});
            skArc(sketch, "E84", {"start": v(15, 120) * mm, "mid": v(0, 135) * mm, "end": v(-15, 120) * mm});
            skPoint(sketch, "E85.endSnap0", {"position": v(0, 90) * mm});
            skLineSegment(sketch, "E86", {"start": v(0, 90) * mm, "end": v(0, 120) * mm, "construction": true});
            skLineSegment(sketch, "E87", {"start": v(-80, 0) * mm, "end": v(80, 0) * mm, "construction": true});
            skLineSegment(sketch, "E88.MirrorCS", {"start": v(-15, -108) * mm, "end": v(-15, -120) * mm});
            skLineSegment(sketch, "E89.MirrorCS", {"start": v(33, -90) * mm, "end": v(15, -108) * mm});
            skLineSegment(sketch, "E90.MirrorCS", {"start": v(15, -108) * mm, "end": v(15, -120) * mm});
            skArc(sketch, "E91.MirrorCS", {"start": v(15, -120) * mm, "mid": v(0, -135) * mm, "end": v(-15, -120) * mm});
            skLineSegment(sketch, "E92.MirrorCS", {"start": v(0, -90) * mm, "end": v(0, -120) * mm, "construction": true});
            skCircle(sketch, "E93.MirrorC", {"center": v(0, -120) * mm, "radius": 6 * mm});
            skLineSegment(sketch, "E94.MirrorCS", {"start": v(-15, -108) * mm, "end": v(-33, -90) * mm});
            skSolve(sketch);
        }
        {
            var Q0;
            Q0=makeQuery(id+"F16.imprint","IMPRINT",FACE,{"disambiguationData":[TD([[makeQuery(id+"F16.imprint","IMPRINT",EDGE,{"derivedFrom":sQuery(id+"F16.wireOp",EDGE,"E79")}),-1.0]])]});
            var Q1;
            Q1=makeQuery(id+"F16.imprint","IMPRINT",FACE,{"disambiguationData":[TD([[makeQuery(id+"F16.imprint","IMPRINT",EDGE,{"derivedFrom":makeQuery(id+"F1.opExtrude","CAP_EDGE",EDGE,{"disambiguationData":[OSD([sQuery(id+"F0.wireOp",EDGE,"E1.left")])],"isStart":true})}),-1.0]])]});
            var Q2;
            Q2=makeQuery(id+"F16.imprint","IMPRINT",FACE,{"disambiguationData":[TD([[makeQuery(id+"F16.imprint","IMPRINT",EDGE,{"derivedFrom":sQuery(id+"F16.wireOp",EDGE,"E88.MirrorCS")}),1.0]])]});
            var Q3;
            Q3=makeQuery(id+"F2.opExtrude","CAP_FACE",FACE,{"disambiguationData":[OSD([sQuery(id+"F0.wireOp",EDGE,"E12"),sQuery(id+"F0.wireOp",EDGE,"E13"),sQuery(id+"F0.wireOp",EDGE,"E14"),sQuery(id+"F0.wireOp",EDGE,"E15"),sQuery(id+"F0.wireOp",EDGE,"E17.filletArc"),sQuery(id+"F0.wireOp",EDGE,"E18.filletArc"),sQuery(id+"F0.wireOp",EDGE,"E19.filletArc"),sQuery(id+"F0.wireOp",EDGE,"E20.filletArc"),sQuery(id+"F0.wireOp",EDGE,"E25.0"),sQuery(id+"F0.wireOp",EDGE,"E25.1"),sQuery(id+"F0.wireOp",EDGE,"E25.2"),sQuery(id+"F0.wireOp",EDGE,"E25.3"),sQuery(id+"F0.wireOp",EDGE,"E25.4"),sQuery(id+"F0.wireOp",EDGE,"E25.5"),sQuery(id+"F0.wireOp",EDGE,"E25.6"),sQuery(id+"F0.wireOp",EDGE,"E25.7")])],"isStart":false});
            extrude(context, id + "F17", {"entities" : qUnion([Q0, Q1, Q2]), "operationType" : NewBodyOperationType.ADD, "endBound" : BoundingType.UP_TO_SURFACE, "depth" : 25 * mm, "endBoundEntityFace" : qUnion([Q3]), "offsetDistance" : 25 * mm});
        }
    });
